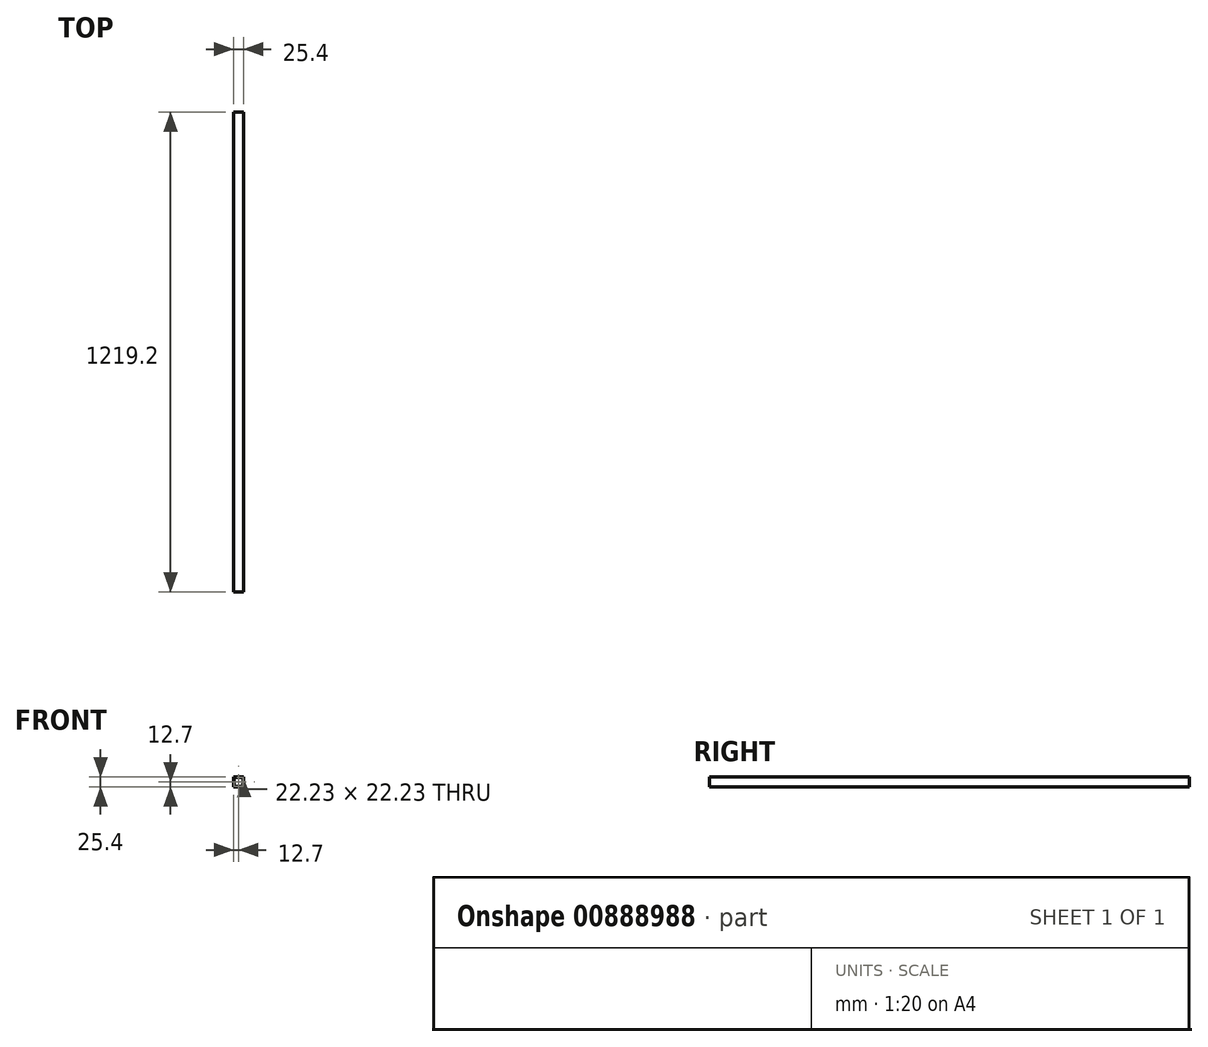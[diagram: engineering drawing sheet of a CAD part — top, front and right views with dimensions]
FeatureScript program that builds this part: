
annotation { "Feature Type Name" : "Feature", "Feature Type Description" : "" }
export const myFeature = defineFeature(function(context is Context, id is Id, definition is map)
    precondition{}
    {
        {
            var Q0;
            Q0=qCreatedBy(makeId("Front.planeOp"),FACE);
            var sketch = newSketch(context, id + "F0", { "sketchPlane" : qUnion([Q0])});
            skLineSegment(sketch, "E0.bottom", {"start": v(0, 0) * mm, "end": v(25.4, 0) * mm});
            skLineSegment(sketch, "E0.top", {"start": v(0, 25.4) * mm, "end": v(25.4, 25.4) * mm});
            skLineSegment(sketch, "E0.left", {"start": v(0, 0) * mm, "end": v(0, 25.4) * mm});
            skLineSegment(sketch, "E0.right", {"start": v(25.4, 0) * mm, "end": v(25.4, 25.4) * mm});
            skLineSegment(sketch, "E1.bottom", {"start": v(1.59, 1.59) * mm, "end": v(23.81, 1.59) * mm});
            skLineSegment(sketch, "E1.top", {"start": v(1.59, 23.81) * mm, "end": v(23.81, 23.81) * mm});
            skLineSegment(sketch, "E1.left", {"start": v(1.59, 1.59) * mm, "end": v(1.59, 23.81) * mm});
            skLineSegment(sketch, "E1.right", {"start": v(23.81, 1.59) * mm, "end": v(23.81, 23.81) * mm});
            skSolve(sketch);
        }
        {
            var Q0;
            Q0=makeQuery(id+"F0.imprint","IMPRINT",FACE,{"disambiguationData":[TD([[makeQuery(id+"F0.imprint","IMPRINT",EDGE,{"derivedFrom":sQuery(id+"F0.wireOp",EDGE,"E0.bottom")}),1.0]])]});
            extrude(context, id + "F1", {"entities" : qUnion([Q0]), "depth" : 1219.2 * mm, "offsetDistance" : 25.4 * mm});
        }
    });
